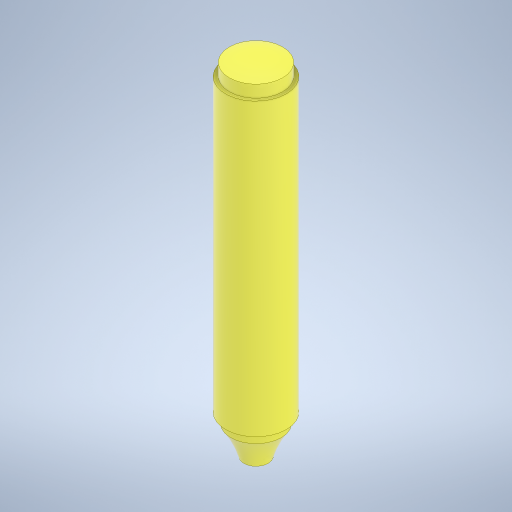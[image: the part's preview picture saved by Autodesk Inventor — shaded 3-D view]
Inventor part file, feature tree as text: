
AUTODESK INVENTOR PART (.ipt)
format: ipt  version: 2023.1 (Build 271208000, 208)  size: 258,560 bytes
history: native  units: mm
features: revolve x1, sketch x1
ambient origin geometry x8: Origin, YZ Plane, XZ Plane, XY Plane, X Axis, Y Axis, Z Axis, Center Point
bodies: Solid1 (feature_tree)
feature tree (2):
  revolve  "Revolution1"  [1 undecoded]
  sketch  "Sketch1"  dims[d0=19.0mm d1=91.0mm d2=15.8mm d3=3.0mm d6=7.65mm d7=9.0mm d8=3.8mm d10=90.0deg]
note: 1 required parameter value undecoded (feature->parameter linkage not recoverable at this tier; creation-order binding heuristic only, values carry confidence <= 0.55)
